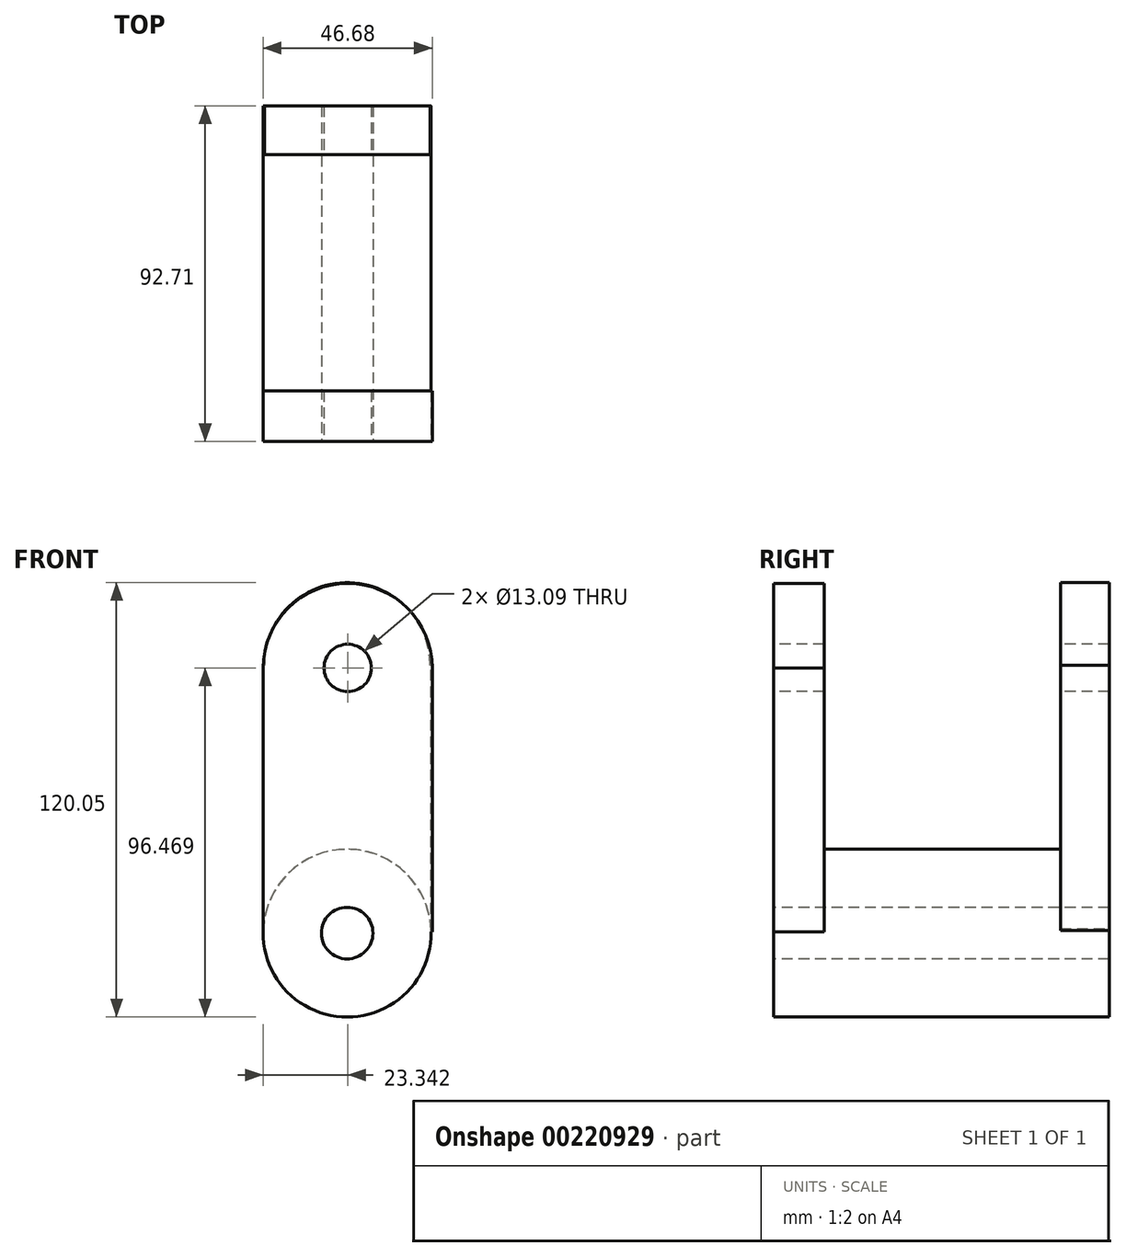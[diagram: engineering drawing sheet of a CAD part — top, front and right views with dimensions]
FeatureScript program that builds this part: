
annotation { "Feature Type Name" : "Feature", "Feature Type Description" : "" }
export const myFeature = defineFeature(function(context is Context, id is Id, definition is map)
    precondition{}
    {
        {
            var Q0;
            Q0=qCreatedBy(makeId("Front.planeOp"),FACE);
            var sketch = newSketch(context, id + "F0", { "sketchPlane" : qUnion([Q0])});
            skCircle(sketch, "E0", {"center": v(-13.33, -39.22) * mm, "radius": 23.19 * mm});
            skSolve(sketch);
        }
        {
            var Q0;
            Q0=makeQuery(id+"F0.imprint","IMPRINT",FACE,{"disambiguationData":[TD([[makeQuery(id+"F0.imprint","IMPRINT",EDGE,{"derivedFrom":sQuery(id+"F0.wireOp",EDGE,"E0")}),1.0]])]});
            extrude(context, id + "F1", {"entities" : qUnion([Q0]), "oppositeDirection" : true, "depth" : 92.7 * mm});
        }
        {
            var Q0;
            Q0=makeQuery(id+"F1.opExtrude","CAP_FACE",FACE,{"disambiguationData":[OSD([sQuery(id+"F0.wireOp",EDGE,"E0")])],"isStart":true});
            var sketch = newSketch(context, id + "F2", { "sketchPlane" : qUnion([Q0])});
            skLineSegment(sketch, "E1.bottom", {"start": v(-36.52, -38.9) * mm, "end": v(10.16, -38.9) * mm});
            skLineSegment(sketch, "E1.top", {"start": v(-36.52, 34.06) * mm, "end": v(10.16, 34.06) * mm});
            skLineSegment(sketch, "E1.left", {"start": v(-36.52, -38.9) * mm, "end": v(-36.52, 34.06) * mm});
            skLineSegment(sketch, "E1.right", {"start": v(10.16, -38.9) * mm, "end": v(10.16, 34.06) * mm});
            skSolve(sketch);
        }
        {
            var Q0;
            Q0=makeQuery(id+"F2.imprint","IMPRINT",FACE,{"disambiguationData":[TD([[makeQuery(id+"F2.imprint","IMPRINT",EDGE,{"derivedFrom":sQuery(id+"F2.wireOp",EDGE,"E1.top")}),-1.0]])]});
            extrude(context, id + "F3", {"entities" : qUnion([Q0]), "operationType" : NewBodyOperationType.ADD, "oppositeDirection" : true, "depth" : 13.97 * mm});
        }
        {
            var Q0;
            {var subQ0=sQuery(id+"F0.wireOp",EDGE,"E0");Q0=makeQuery(id+"F3.boolean.opBoolean","MERGE",FACE,{"derivedFrom":[makeQuery(id+"F1.opExtrude","CAP_FACE",FACE,{"disambiguationData":[OSD([subQ0])],"isStart":true}),makeQuery(id+"F3.opExtrude","CAP_FACE",FACE,{"disambiguationData":[OSD([subQ0,sQuery(id+"F2.wireOp",EDGE,"E1.bottom"),sQuery(id+"F2.wireOp",EDGE,"E1.top"),sQuery(id+"F2.wireOp",EDGE,"E1.left"),sQuery(id+"F2.wireOp",EDGE,"E1.right")])],"isStart":true})]});}
            var sketch = newSketch(context, id + "F4", { "sketchPlane" : qUnion([Q0])});
            skCircle(sketch, "E2", {"center": v(-13.18, 34.06) * mm, "radius": 23.32 * mm});
            skSolve(sketch);
        }
        {
            var Q0;
            {var subQ0=sQuery(id+"F4.wireOp",EDGE,"E2");var subQ1=makeQuery(id+"F3.opExtrude","CAP_EDGE",EDGE,{"disambiguationData":[OSD([sQuery(id+"F2.wireOp",EDGE,"E1.top")])],"isStart":true});var subQ2=makeQuery(id+"F4.imprint","INTERSECT",VERTEX,{"disambiguationData":[OD(0.0)],"derivedFrom":[subQ1,subQ0]});Q0=makeQuery(id+"F4.imprint","IMPRINT",FACE,{"disambiguationData":[TD([[makeQuery(id+"F4.imprint","IMPRINT",EDGE,{"disambiguationData":[TD([[subQ2,1.0]])],"derivedFrom":subQ0}),1.0]])]});}
            extrude(context, id + "F5", {"entities" : qUnion([Q0]), "operationType" : NewBodyOperationType.ADD, "oppositeDirection" : true, "depth" : 13.97 * mm});
        }
        {
            var Q0;
            Q0=makeQuery(id+"F1.opExtrude","CAP_FACE",FACE,{"disambiguationData":[OSD([sQuery(id+"F0.wireOp",EDGE,"E0")])],"isStart":false});
            var sketch = newSketch(context, id + "F6", { "sketchPlane" : qUnion([Q0])});
            skLineSegment(sketch, "E3.bottom", {"start": v(-9.84, -38.46) * mm, "end": v(36.48, -38.46) * mm});
            skLineSegment(sketch, "E3.top", {"start": v(-9.84, 34.75) * mm, "end": v(36.48, 34.75) * mm});
            skLineSegment(sketch, "E3.left", {"start": v(-9.84, -38.46) * mm, "end": v(-9.84, 34.75) * mm});
            skLineSegment(sketch, "E3.right", {"start": v(36.48, -38.46) * mm, "end": v(36.48, 34.75) * mm});
            skSolve(sketch);
        }
        {
            var Q0;
            {var subQ0=sQuery(id+"F6.wireOp",EDGE,"E3.top");Q0=makeQuery(id+"F6.imprint","IMPRINT",FACE,{"disambiguationData":[TD([[makeQuery(id+"F6.imprint","IMPRINT",EDGE,{"derivedFrom":subQ0}),-1.0]])]});}
            extrude(context, id + "F7", {"entities" : qUnion([Q0]), "operationType" : NewBodyOperationType.ADD, "oppositeDirection" : true, "depth" : 13.46 * mm});
        }
        {
            var Q0;
            {var subQ0=sQuery(id+"F0.wireOp",EDGE,"E0");Q0=makeQuery(id+"F7.boolean.opBoolean","MERGE",FACE,{"derivedFrom":[makeQuery(id+"F1.opExtrude","CAP_FACE",FACE,{"disambiguationData":[OSD([subQ0])],"isStart":false}),makeQuery(id+"F7.opExtrude","CAP_FACE",FACE,{"disambiguationData":[OSD([subQ0,sQuery(id+"F6.wireOp",EDGE,"E3.top"),sQuery(id+"F6.wireOp",EDGE,"E3.left"),sQuery(id+"F6.wireOp",EDGE,"E3.right")])],"isStart":true})]});}
            var sketch = newSketch(context, id + "F8", { "sketchPlane" : qUnion([Q0])});
            skCircle(sketch, "E4", {"center": v(13.32, 34.75) * mm, "radius": 22.89 * mm});
            skSolve(sketch);
        }
        {
            var Q0;
            {var subQ0=sQuery(id+"F8.wireOp",EDGE,"E4");var subQ1=makeQuery(id+"F7.opExtrude","CAP_EDGE",EDGE,{"disambiguationData":[OSD([sQuery(id+"F6.wireOp",EDGE,"E3.top")])],"isStart":true});var subQ2=makeQuery(id+"F8.imprint","INTERSECT",VERTEX,{"disambiguationData":[OD(0.0)],"derivedFrom":[subQ1,subQ0]});Q0=makeQuery(id+"F8.imprint","IMPRINT",FACE,{"disambiguationData":[TD([[makeQuery(id+"F8.imprint","IMPRINT",EDGE,{"disambiguationData":[TD([[subQ2,1.0]])],"derivedFrom":subQ0}),1.0]])]});}
            extrude(context, id + "F9", {"entities" : qUnion([Q0]), "operationType" : NewBodyOperationType.ADD, "oppositeDirection" : true, "depth" : 13.46 * mm});
        }
        {
            var Q0;
            {var subQ0=sQuery(id+"F2.wireOp",EDGE,"E1.top");var subQ1=sQuery(id+"F0.wireOp",EDGE,"E0");Q0=makeQuery(id+"F5.boolean.opBoolean","MERGE",FACE,{"derivedFrom":[makeQuery(id+"F3.boolean.opBoolean","MERGE",FACE,{"derivedFrom":[makeQuery(id+"F1.opExtrude","CAP_FACE",FACE,{"disambiguationData":[OSD([subQ1])],"isStart":true}),makeQuery(id+"F3.opExtrude","CAP_FACE",FACE,{"disambiguationData":[OSD([subQ1,sQuery(id+"F2.wireOp",EDGE,"E1.bottom"),subQ0,sQuery(id+"F2.wireOp",EDGE,"E1.left"),sQuery(id+"F2.wireOp",EDGE,"E1.right")])],"isStart":true})]}),makeQuery(id+"F5.opExtrude","CAP_FACE",FACE,{"disambiguationData":[OSD([subQ0,sQuery(id+"F4.wireOp",EDGE,"E2")])],"isStart":true})]});}
            var sketch = newSketch(context, id + "F10", { "sketchPlane" : qUnion([Q0])});
            skCircle(sketch, "E5", {"center": v(-13.33, -39.22) * mm, "radius": 7.13 * mm});
            skSolve(sketch);
        }
        {
            var Q0;
            Q0=makeQuery(id+"F10.imprint","IMPRINT",FACE,{"disambiguationData":[TD([[makeQuery(id+"F10.imprint","IMPRINT",EDGE,{"derivedFrom":sQuery(id+"F10.wireOp",EDGE,"E5")}),1.0]])]});
            extrude(context, id + "F11", {"entities" : qUnion([Q0]), "operationType" : NewBodyOperationType.REMOVE, "endBound" : BoundingType.THROUGH_ALL, "oppositeDirection" : true, "depth" : 25.4 * mm});
        }
        {
            var Q0;
            {var subQ0=sQuery(id+"F2.wireOp",EDGE,"E1.top");var subQ1=sQuery(id+"F0.wireOp",EDGE,"E0");Q0=makeQuery(id+"F5.boolean.opBoolean","MERGE",FACE,{"derivedFrom":[makeQuery(id+"F3.boolean.opBoolean","MERGE",FACE,{"derivedFrom":[makeQuery(id+"F1.opExtrude","CAP_FACE",FACE,{"disambiguationData":[OSD([subQ1])],"isStart":true}),makeQuery(id+"F3.opExtrude","CAP_FACE",FACE,{"disambiguationData":[OSD([subQ1,sQuery(id+"F2.wireOp",EDGE,"E1.bottom"),subQ0,sQuery(id+"F2.wireOp",EDGE,"E1.left"),sQuery(id+"F2.wireOp",EDGE,"E1.right")])],"isStart":true})]}),makeQuery(id+"F5.opExtrude","CAP_FACE",FACE,{"disambiguationData":[OSD([subQ0,sQuery(id+"F4.wireOp",EDGE,"E2")])],"isStart":true})]});}
            var sketch = newSketch(context, id + "F12", { "sketchPlane" : qUnion([Q0])});
            skCircle(sketch, "E6", {"center": v(-13.18, 34.06) * mm, "radius": 6.54 * mm});
            skSolve(sketch);
        }
        {
            var Q0;
            Q0=makeQuery(id+"F12.imprint","IMPRINT",FACE,{"disambiguationData":[TD([[makeQuery(id+"F12.imprint","IMPRINT",EDGE,{"derivedFrom":sQuery(id+"F12.wireOp",EDGE,"E6")}),1.0]])]});
            extrude(context, id + "F13", {"entities" : qUnion([Q0]), "operationType" : NewBodyOperationType.REMOVE, "endBound" : BoundingType.THROUGH_ALL, "oppositeDirection" : true, "depth" : 25.4 * mm});
        }
    });
